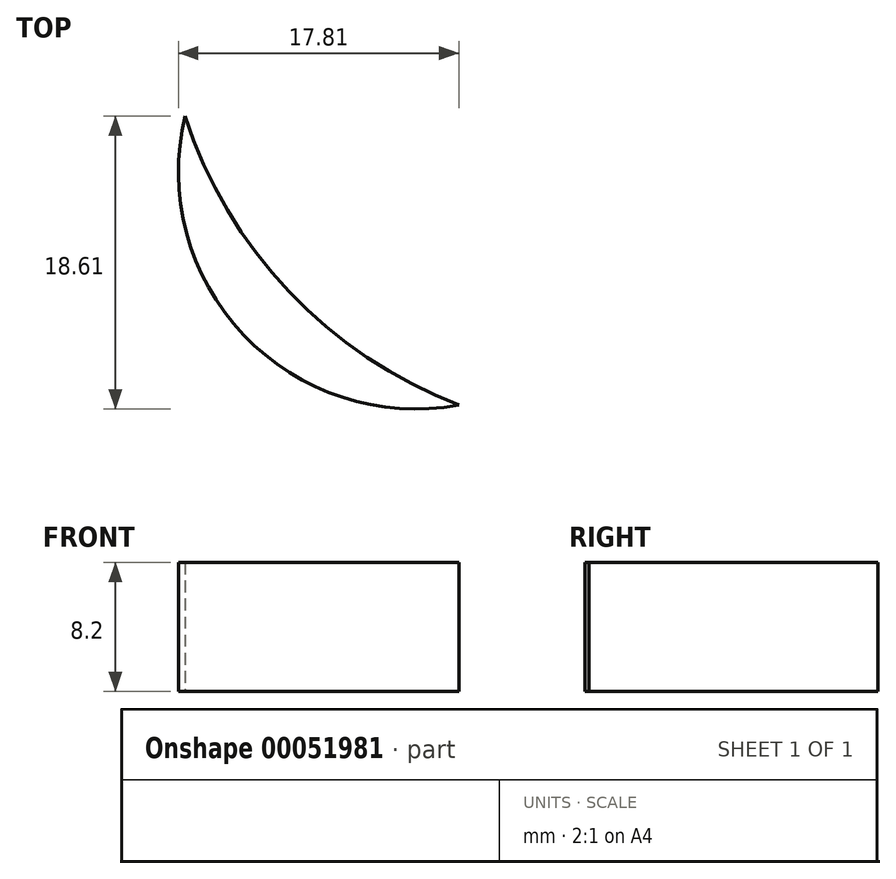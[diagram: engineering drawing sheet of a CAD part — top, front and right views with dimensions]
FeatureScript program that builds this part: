
annotation { "Feature Type Name" : "Feature", "Feature Type Description" : "" }
export const myFeature = defineFeature(function(context is Context, id is Id, definition is map)
    precondition{}
    {
        {
            var Q0;
            Q0=qCreatedBy(makeId("Top.planeOp"),FACE);
            var sketch = newSketch(context, id + "F0", { "sketchPlane" : qUnion([Q0])});
            skArc(sketch, "E0", {"start": v(-55.72, 29.15) * mm, "mid": v(-52, 15.25) * mm, "end": v(-38.33, 10.79) * mm});
            skArc(sketch, "E1", {"start": v(-55.72, 29.15) * mm, "mid": v(-49.1, 18) * mm, "end": v(-38.33, 10.79) * mm});
            skSolve(sketch);
        }
        {
            var Q0;
            Q0 = qSketchRegion(id + "F0", true);
            extrude(context, id + "F1", {"entities" : qUnion([Q0]), "depth" : 8.2 * mm});
        }
    });
